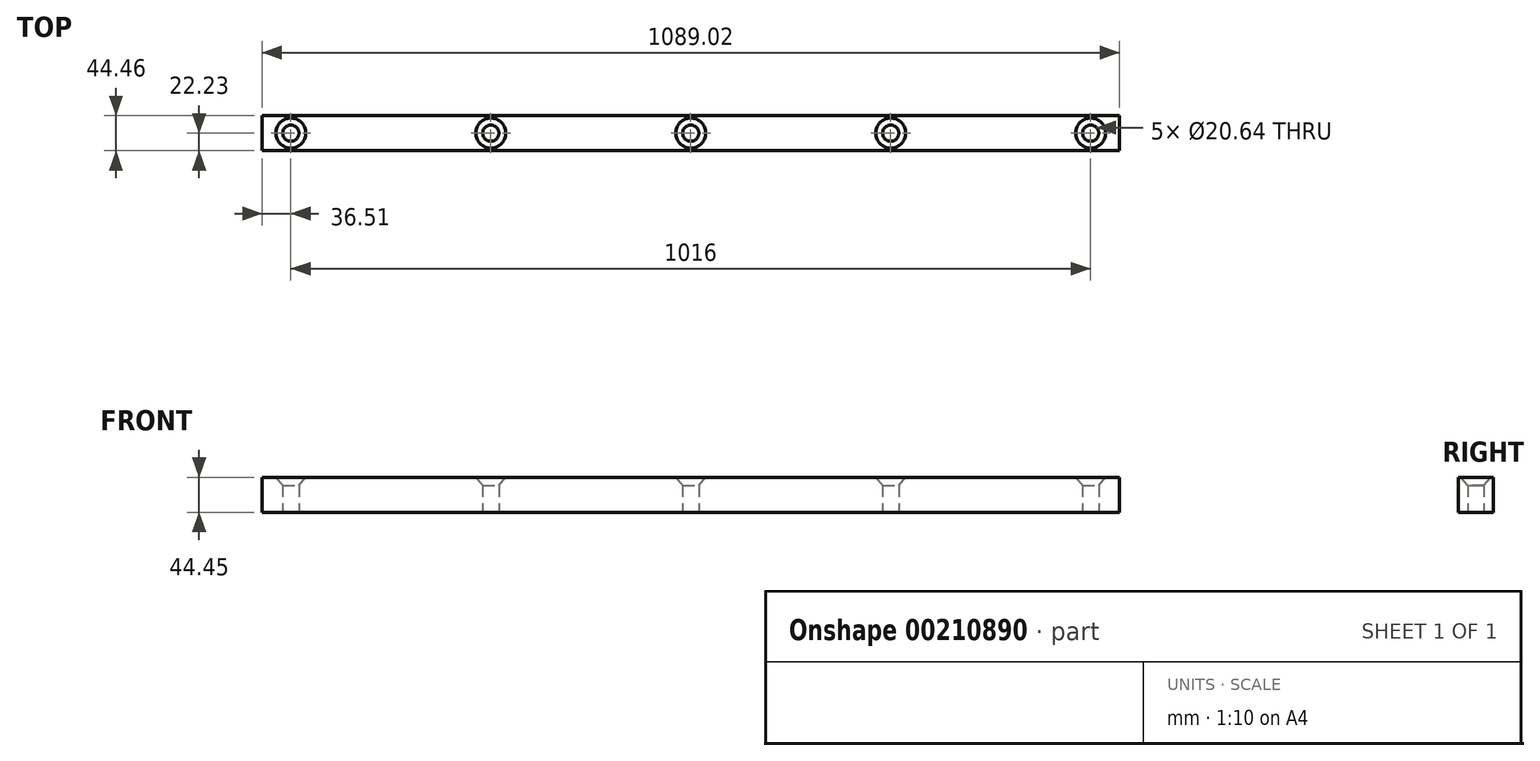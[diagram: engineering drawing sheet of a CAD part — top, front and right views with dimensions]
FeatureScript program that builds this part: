
annotation { "Feature Type Name" : "Feature", "Feature Type Description" : "" }
export const myFeature = defineFeature(function(context is Context, id is Id, definition is map)
    precondition{}
    {
        {
            var Q0;
            Q0=qCreatedBy(makeId("Right.planeOp"),FACE);
            var sketch = newSketch(context, id + "F0", { "sketchPlane" : qUnion([Q0])});
            skLineSegment(sketch, "E0.bottom", {"start": v(-22.22, 0) * mm, "end": v(22.22, 0) * mm});
            skLineSegment(sketch, "E0.top", {"start": v(-22.23, 44.45) * mm, "end": v(22.22, 44.45) * mm});
            skLineSegment(sketch, "E0.left", {"start": v(-22.23, 0) * mm, "end": v(-22.23, 44.45) * mm});
            skLineSegment(sketch, "E0.right", {"start": v(22.22, 0) * mm, "end": v(22.22, 44.45) * mm});
            skSolve(sketch);
        }
        {
            var Q0;
            Q0 = qSketchRegion(id + "F0", true);
            extrude(context, id + "F1", {"entities" : qUnion([Q0]), "depth" : 1089.02 * mm, "symmetric" : true});
        }
        {
            var Q0;
            Q0=makeQuery(id+"F1.opExtrude","SWEPT_FACE",FACE,{"disambiguationData":[OSD([sQuery(id+"F0.wireOp",EDGE,"E0.top")])]});
            var sketch = newSketch(context, id + "F2", { "sketchPlane" : qUnion([Q0])});
            skPoint(sketch, "E1", {"position": v(0, 0) * mm});
            skPoint(sketch, "E2", {"position": v(-508, 0) * mm});
            skPoint(sketch, "E3", {"position": v(-254, 0) * mm});
            skPoint(sketch, "E4", {"position": v(254, 0) * mm});
            skPoint(sketch, "E5", {"position": v(508, 0) * mm});
            skSolve(sketch);
        }
        {
            var Q0;
            Q0=sQuery(id+"F2.wireOp",VERTEX,"E2");
            var Q1;
            Q1=sQuery(id+"F2.wireOp",VERTEX,"E3");
            var Q2;
            Q2=sQuery(id+"F2.wireOp",VERTEX,"E1");
            var Q3;
            Q3=sQuery(id+"F2.wireOp",VERTEX,"E4");
            var Q4;
            Q4=sQuery(id+"F2.wireOp",VERTEX,"E5");
            var Q5;
            Q5=makeQuery(id+"F1.opExtrude","SWEPT_BODY",BODY,{"disambiguationData":[OSD([sQuery(id+"F0.wireOp",EDGE,"E0.bottom"),sQuery(id+"F0.wireOp",EDGE,"E0.top"),sQuery(id+"F0.wireOp",EDGE,"E0.left"),sQuery(id+"F0.wireOp",EDGE,"E0.right")])]});
            hole(context, id + "F3", {"style" : HoleStyle.C_SINK, "endStyle" : HoleEndStyle.THROUGH, "holeDiameter" : 20.64 * mm, "cSinkDiameter" : 38.1 * mm, "cSinkAngle" : 82 * degree, "locations" : qUnion([Q0, Q1, Q2, Q3, Q4]), "scope" : qUnion([Q5]), "isTappedThrough" : true, "startStyle" : HoleStartStyle.PART});
        }
    });
